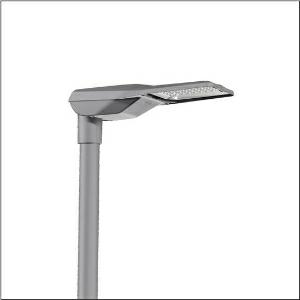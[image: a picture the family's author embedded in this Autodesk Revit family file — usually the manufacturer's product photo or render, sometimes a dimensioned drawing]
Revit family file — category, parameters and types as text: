
# Revit family: streetlight_sl_21_iq_mini___st1_0a_5xe2d31g08gb_f91a
name_source: partatom
category: Lighting Fixtures
units: mm (PartAtom-declared; Revit-internal decimal feet)

## family parameters
Cut with Voids When Loaded = No
Host = Face
Light Source = No
Part Type = Normal
Room Calculation Point = No
Round Connector Dimension = Use Diameter
Shared = No

## types (1)
- --- (1 x LED, 5680 lm, 37.1 W, 3000K)
    Apparent Load = 37 VA
    CIE Flux Codes = 37 72 97 100 100
    Color Rendering = 70
    Color Temperature = 3000K
    Default Elevation = 1800 mm
    Description = Streetlight SL 21 iQ mini, mast luminaire, primary light control with lens, of PMMA, primary optical cover: cover, of toughened safety glass, transparent, light distribution: ST1.0a, light emission: direct distribution, primary light characteristic: asymmetric, installation type: post-top, side-entry, LED, High Power LED, rated luminous flux: 5.680lm, luminous efficacy: 153lm/W, light colour: 730, colour temperature: 3000K, control gear: iQ Street-Remote, control: Street-Remote, Auto-Match, Temp-Guard, Lumen-Switch, Night-Set, Smart-Wire, Light-Fading, Desk-Remote (wireless, voltage-free reading and setting of iQ features in the workshop via application-optimized NFC function/RFID function), optimised constant luminous flux control (CLO 2.0), pre-setting: linear dimming characteristic, mains connection: 220..240V, AC, 50/60Hz, start of lifetime: 37W, end of service life: 39W, reduction: 18W, luminaire housing, of diecast aluminium, powder-coated, SITECO metallic grey (DB 702S), corrosivity category C5 high according to DIN EN ISO 12944, please order mast flange separately, inclination adjustable: 0°, 5°, 10°, 15°, sealing non-destructively replaceable, multi-level sealing system, length: 628mm, width: 235mm, height: 110mm, mast flange for spigot size: 42mm (side-entry): 5XC10008XM4, 60/48mm (side-entry/post-top): 5XC10108XM2, 76/60mm (side-entry/post-top): 5XC10108XM1, mounting height: 4..8m, protection rating (complete): IP66, insulation class (complete): insulation class II (safety insulation), certification: CE, ENEC, ENEC+, VDE, impact resistance: IK10, permissible operating ambient temperature for outdoor applications: -40..+50°C, standard-compliant lighting for roads and squares, packaging unit: 1 piece

Light Distribution: ST1.0a
    Height = 110 mm
    Lamp = 1 x LED
    Lamp Light Flux = 5680 lm
    Lamp Power = 37.1 W
    Lamp count = 1
    Length = 625 mm
    Luminous efficacy = 153 lm/W
    Manufacturer = Siteco
    ModVariant = No
    Model = 5XE2D31G08GB
    Number of Poles = 1
    OnlyDefault = Yes
    Power Factor = 1
    Product Name = Streetlight SL 21 iQ mini | ST1.0a
    Product group = mast luminaire | pylon top
    ProductGroupID = 6100
    Protection Class = Protection class II
    Protection Degree = IP 66
    RLX_Detail_Level = 1
    RLX_Emergency_Light_Flux = 0 lm
    RLX_Emergency_Type = 0
    RLX_Emergency_Type_DB = No
    RlxData = <blob elided: 26349 chars, md5=742063f9>
    Socket = socket
    Standby Power = 0 W
    System Light Flux = 5680 lm
    System Power = 37 W
    Type Comments = factory setting: luminous flux: 100 % | dim-lin: 254 | 385 mA
    Type Image = l_1003519.jpg
    URL = http://relux.com
    VarID = @adj_186381
    Voltage = 0 V
    Weight = 0.00 kg
    Width = 234 mm

## geometry (parser evidence)
native form markers: Blend x4, Sweep x12
no freeform markers — native parametric forms only
